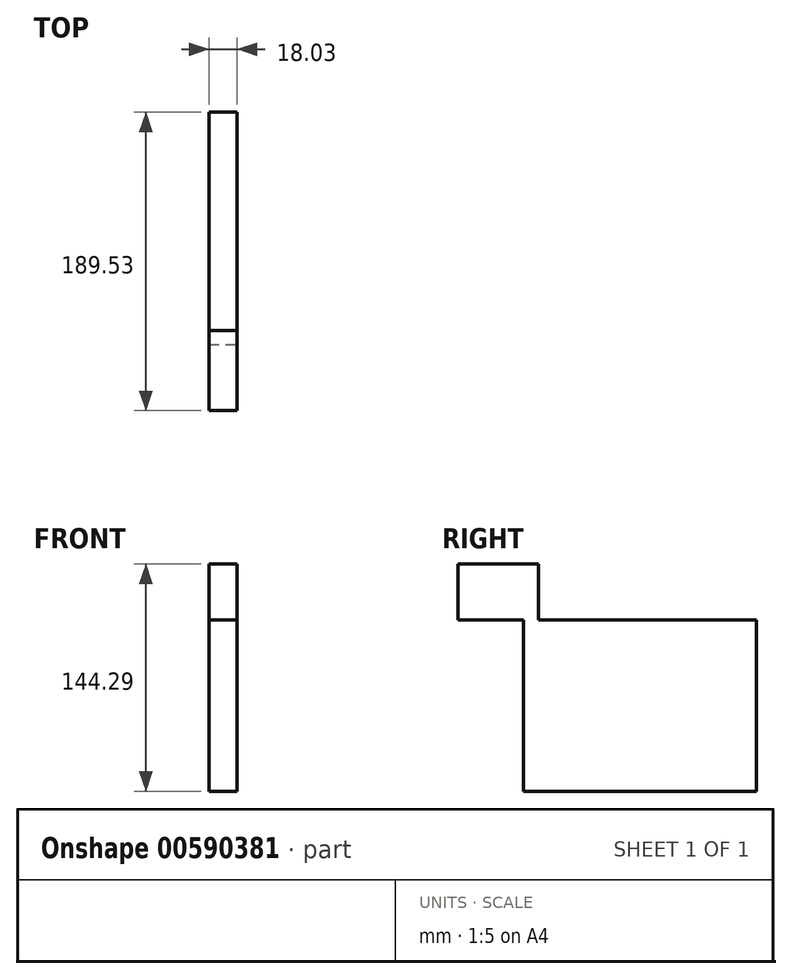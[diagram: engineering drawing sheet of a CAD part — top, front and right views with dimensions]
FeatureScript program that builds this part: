
annotation { "Feature Type Name" : "Feature", "Feature Type Description" : "" }
export const myFeature = defineFeature(function(context is Context, id is Id, definition is map)
    precondition{}
    {
        {
            var Q0;
            Q0=qCreatedBy(makeId("Right.planeOp"),FACE);
            var sketch = newSketch(context, id + "F0", { "sketchPlane" : qUnion([Q0])});
            skLineSegment(sketch, "E0.bottom", {"start": v(-73.06, 71.2) * mm, "end": v(74.84, 71.2) * mm});
            skLineSegment(sketch, "E0.top", {"start": v(-73.06, -37.59) * mm, "end": v(74.84, -37.59) * mm});
            skLineSegment(sketch, "E0.left", {"start": v(-73.06, 71.2) * mm, "end": v(-73.06, -37.59) * mm});
            skLineSegment(sketch, "E0.right", {"start": v(74.84, 71.2) * mm, "end": v(74.84, -37.59) * mm});
            skLineSegment(sketch, "E1.bottom", {"start": v(0, 8.7) * mm, "end": v(0, 8.7) * mm});
            skLineSegment(sketch, "E1.top", {"start": v(0, 0) * mm, "end": v(0, 0) * mm});
            skLineSegment(sketch, "E1.left", {"start": v(0, 8.7) * mm, "end": v(0, 0) * mm});
            skLineSegment(sketch, "E1.right", {"start": v(0, 8.7) * mm, "end": v(0, 0) * mm});
            skLineSegment(sketch, "E2.bottom", {"start": v(74.84, -37.59) * mm, "end": v(-78.98, -37.59) * mm});
            skLineSegment(sketch, "E2.top", {"start": v(74.84, -37.59) * mm, "end": v(-78.98, -37.59) * mm});
            skLineSegment(sketch, "E2.left", {"start": v(74.84, -37.59) * mm, "end": v(74.84, -37.59) * mm});
            skLineSegment(sketch, "E2.right", {"start": v(-78.98, -37.59) * mm, "end": v(-78.98, -37.59) * mm});
            skLineSegment(sketch, "E3.bottom", {"start": v(-114.69, 106.7) * mm, "end": v(-63.67, 106.7) * mm});
            skLineSegment(sketch, "E3.top", {"start": v(-114.69, 71.2) * mm, "end": v(-63.67, 71.2) * mm});
            skLineSegment(sketch, "E3.left", {"start": v(-114.69, 106.7) * mm, "end": v(-114.69, 71.2) * mm});
            skLineSegment(sketch, "E3.right", {"start": v(-63.67, 106.7) * mm, "end": v(-63.67, 71.2) * mm});
            skSolve(sketch);
        }
        {
            var Q0;
            Q0 = qSketchRegion(id + "F0", true);
            extrude(context, id + "F1", {"entities" : qUnion([Q0]), "depth" : 18.03 * mm, "offsetDistance" : 25.4 * mm});
        }
    });
